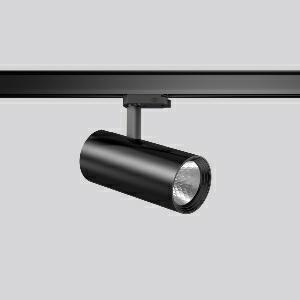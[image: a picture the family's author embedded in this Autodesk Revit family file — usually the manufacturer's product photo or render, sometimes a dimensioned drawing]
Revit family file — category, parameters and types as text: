
# Revit family: deecos_s_mini_742203_003_4a21
name_source: partatom
category: Lighting Fixtures
units: mm (PartAtom-declared; Revit-internal decimal feet)

## family parameters
Cut with Voids When Loaded = No
Host = Face
Light Source = No
Part Type = Normal
Room Calculation Point = No
Round Connector Dimension = Use Diameter
Shared = No

## types (1)
- DEECOS S mini (1 x LED Modul 930, 3550 lm, 3000)
    Apparent Load = 29 VA
    Approval mark = CE
    CIE Flux Codes = 100 100 100 100 100
    Color Rendering = 90
    Color Temperature = 3000
    Default Elevation = 1800 mm
    Description = Series: DEECOS S mini
LED surface-mounted projector in modern design with no visible cooling ribs. Housing: die-cast aluminium, powder-coated. Rotation range: 356°. Swivel range: 90°. Black plastic ring and recessed LED to prevent glare from the side. Optical assembly with reflector made of MIRO-Silver with 98% total light reflection for outstanding efficiency - can be changed without tools. Best colour rendering index Ra>90. With multi adaptor for 3-circuit tracks 230 V. Suitable for Track on ceiling, Wall track. High quality converter without flickering and stroboscopic effect. The following accessories can be mounted without use of tools: interchangeable lenses, decorative glasses, honeycomb louvre, clear and frosted diffusers, white interchangeable plastic ring. 
Colour: deep black, matt (RAL 9005)
Diameter: 87 mm
Height: 214 mm
Lamp: LED
Socket: without socket
Colour temperature: 3000K
Colour rendering index (CRI): 92
System power: 29 W
Rated luminous flux: 3550 lm
Luminous efficiency: 122 lm/W
Control gear: Regulated power supply
Protection class: I
Type of protection: IP 20
    Height = 214 mm
    Lamp = 1 x LED Modul 930
    Lamp Light Flux = 3550 lm
    Lamp count = 1
    Length = 87 mm
    Lifetime = 50000 h
    Luminous efficacy = 122 lm/W
    Manufacturer = RZB
    ModVariant = No
    Model = 742203.003
    Mounting Place = Ceiling
    Mounting Type = Rail mounted
    Number of Poles = 1
    OnlyDefault = Yes
    Power Factor = 1
    Product Name = DEECOS S mini
    Product group = Track mounted projectors
    ProductGroupID = 301
    Protection Class = Protection class I
    Protection Degree = IP 20
    RLX_Detail_Level = 1
    RLX_Emergency_Light_Flux = 0 lm
    RLX_Emergency_Type = 0
    RLX_Emergency_Type_DB = No
    RlxData = <blob elided: 38717 chars, md5=4a271f14>
    Socket = socket
    Standby Power = 0 W
    System Light Flux = 3550 lm
    System Power = 29 W
    Type Comments = Product without accessories
    Type Image = 741926.003.jpg
    URL = http://relux.com
    VarID = ---
    Voltage = 230 V
    Voltage Range = 220-240 V
    Weight = 0.00 kg
    Width = 0 mm  [stored 0 ft]

note: [stored X ft] marks values corroborated as IEEE doubles in the binary element streams (Revit-internal decimal feet)

## geometry (parser evidence)
native form markers: Blend x4, Sweep x12
no freeform markers — native parametric forms only
